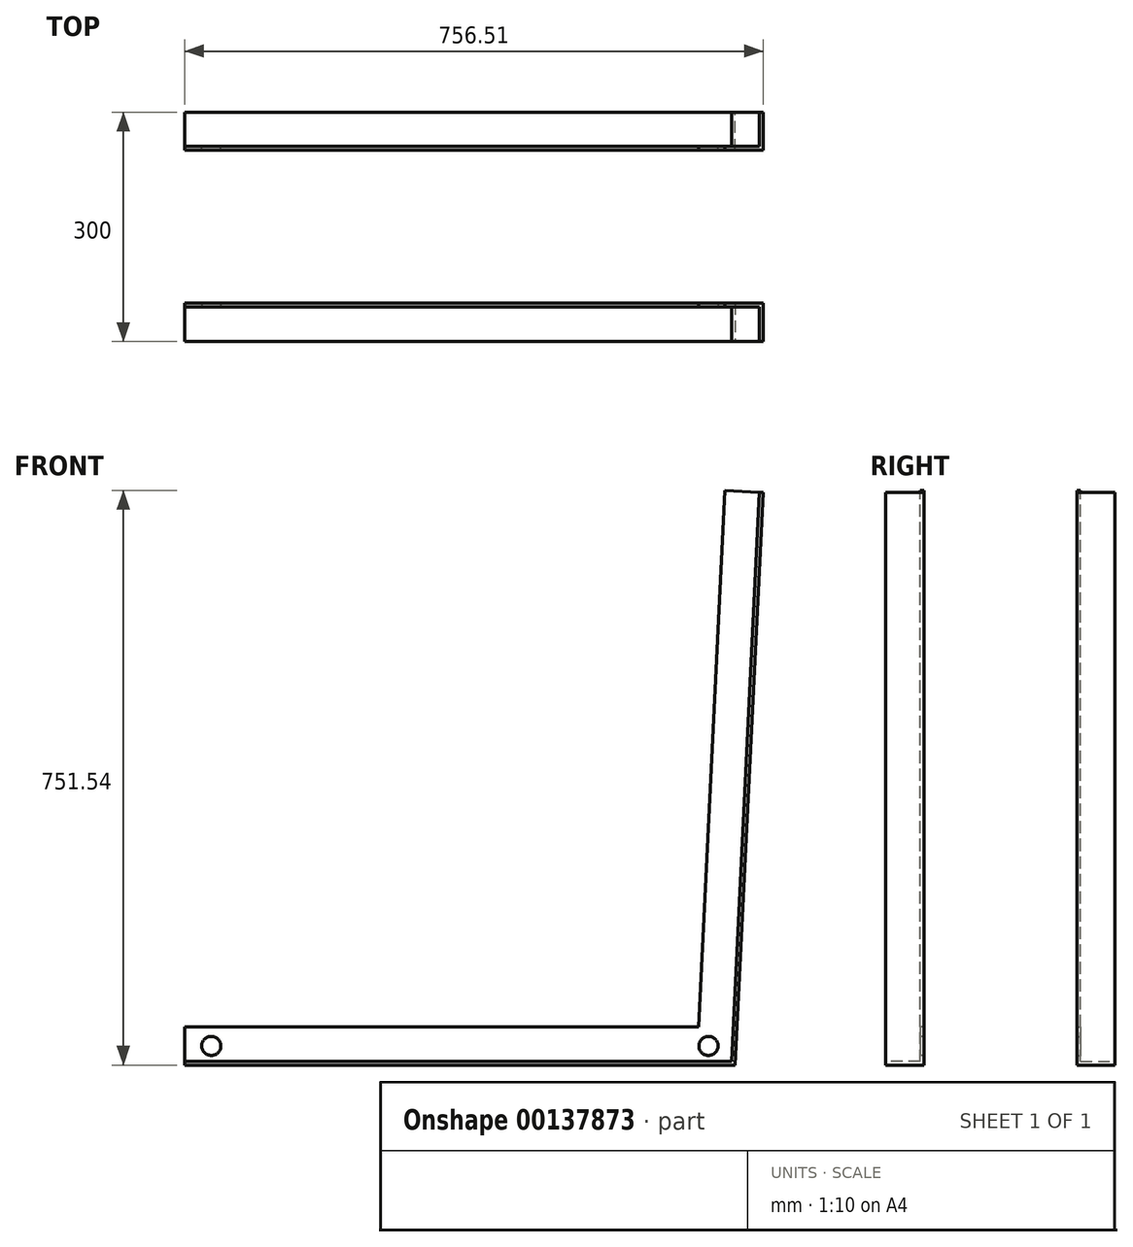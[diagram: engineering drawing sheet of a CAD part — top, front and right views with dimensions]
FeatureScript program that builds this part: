
annotation { "Feature Type Name" : "Feature", "Feature Type Description" : "" }
export const myFeature = defineFeature(function(context is Context, id is Id, definition is map)
    precondition{}
    {
        {
            var Q0;
            Q0=qCreatedBy(makeId("Right.planeOp"),FACE);
            var sketch = newSketch(context, id + "F0", { "sketchPlane" : qUnion([Q0])});
            skLineSegment(sketch, "E0", {"start": v(100, 50) * mm, "end": v(105, 50) * mm});
            skLineSegment(sketch, "E1", {"start": v(105, 50) * mm, "end": v(105, 5) * mm});
            skLineSegment(sketch, "E2", {"start": v(105, 5) * mm, "end": v(150, 5) * mm});
            skLineSegment(sketch, "E3", {"start": v(150, 5) * mm, "end": v(150, 0) * mm});
            skLineSegment(sketch, "E4", {"start": v(100, 50) * mm, "end": v(100, 0) * mm});
            skLineSegment(sketch, "E5", {"start": v(100, 0) * mm, "end": v(150, 0) * mm});
            skSolve(sketch);
        }
        {
            var Q0;
            Q0=qCreatedBy(makeId("Front.planeOp"),FACE);
            var Q1;
            Q1=sQuery(id+"F0.wireOp",VERTEX,"E5.start");
            cPlane(context, id + "F1", {"entities" : qUnion([Q0, Q1]), "cplaneType" : CPlaneType.PLANE_POINT, "offset" : 25 * mm, "width" : 150 * mm, "height" : 150 * mm});
        }
        {
            var Q0;
            Q0=qCreatedBy(id+"F1.planeOp",FACE);
            var sketch = newSketch(context, id + "F2", { "sketchPlane" : qUnion([Q0])});
            skLineSegment(sketch, "E6", {"start": v(0, 0) * mm, "end": v(720, 0) * mm});
            skLineSegment(sketch, "E7", {"start": v(720, 0) * mm, "end": v(756.5, 749.11) * mm});
            skSolve(sketch);
        }
        {
            var Q0;
            Q0=makeQuery(id+"F0.imprint","IMPRINT",FACE,{"disambiguationData":[TD([[makeQuery(id+"F0.imprint","IMPRINT",EDGE,{"derivedFrom":sQuery(id+"F0.wireOp",EDGE,"E0")}),-1.0]])]});
            var Q1;
            Q1=sQuery(id+"F2.wireOp",EDGE,"E6");
            var Q2;
            Q2=sQuery(id+"F2.wireOp",EDGE,"E7");
            sweep(context, id + "F3", {"profiles" : qUnion([Q0]), "path" : qUnion([Q1, Q2])});
        }
        {
            var Q0;
            Q0=makeQuery(id+"F7.opPattern","COPY",VERTEX,{"derivedFrom":makeQuery(id+"F3.opSweep","MID_CAP_VERTEX",VERTEX,{"disambiguationData":[OSD([sQuery(id+"F0.wireOp",EDGE,"E4"),sQuery(id+"F0.wireOp",EDGE,"E5"),sQuery(id+"F2.wireOp",EDGE,"E6")])],"capPos":1.0}),"instanceName":"1"});
            var Q1;
            Q1=makeQuery(id+"F7.opPattern","COPY",EDGE,{"derivedFrom":makeQuery(id+"F3.opSweep","SWEPT_EDGE",EDGE,{"disambiguationData":[OSD([sQuery(id+"F0.wireOp",EDGE,"E4"),sQuery(id+"F0.wireOp",EDGE,"E5"),sQuery(id+"F2.wireOp",EDGE,"E6")])]}),"instanceName":"1"});
            var Q2;
            Q2=makeQuery(id+"F3.opSweep","MID_CAP_VERTEX",VERTEX,{"disambiguationData":[OSD([sQuery(id+"F0.wireOp",EDGE,"E4"),sQuery(id+"F0.wireOp",EDGE,"E5"),sQuery(id+"F2.wireOp",EDGE,"E6")])],"capPos":1.0});
            var Q3;
            Q3=makeQuery(id+"F3.opSweep","SWEPT_EDGE",EDGE,{"disambiguationData":[OSD([sQuery(id+"F0.wireOp",EDGE,"E4"),sQuery(id+"F0.wireOp",EDGE,"E5"),sQuery(id+"F2.wireOp",EDGE,"E6")])]});
            cPlane(context, id + "F4", {"entities" : qUnion([Q0, Q1, Q2, Q3]), "cplaneType" : CPlaneType.LINE_POINT, "offset" : 25 * mm, "width" : 150 * mm, "height" : 150 * mm});
        }
        {
            var Q0;
            Q0=makeQuery(id+"F3.opSweep","SWEPT_FACE",FACE,{"disambiguationData":[OSD([sQuery(id+"F0.wireOp",EDGE,"E4"),sQuery(id+"F2.wireOp",EDGE,"E6")])]});
            var sketch = newSketch(context, id + "F5", { "sketchPlane" : qUnion([Q0])});
            skPoint(sketch, "E8", {"position": v(35, 25) * mm});
            skPoint(sketch, "E9", {"position": v(685, 25) * mm});
            skSolve(sketch);
        }
        {
            var Q0;
            Q0=sQuery(id+"F5.wireOp",VERTEX,"E8");
            var Q1;
            Q1=sQuery(id+"F5.wireOp",VERTEX,"E9");
            var Q2;
            Q2=makeQuery(id+"F3.opSweep","SWEPT_BODY",BODY,{"disambiguationData":[OSD([sQuery(id+"F0.wireOp",EDGE,"E0"),sQuery(id+"F0.wireOp",EDGE,"E1"),sQuery(id+"F0.wireOp",EDGE,"E2"),sQuery(id+"F0.wireOp",EDGE,"E3"),sQuery(id+"F0.wireOp",EDGE,"E4"),sQuery(id+"F0.wireOp",EDGE,"E5"),sQuery(id+"F2.wireOp",EDGE,"E7")])]});
            hole(context, id + "F6", {"style" : HoleStyle.SIMPLE, "endStyle" : HoleEndStyle.THROUGH, "holeDiameter" : 25 * mm, "locations" : qUnion([Q0, Q1]), "scope" : qUnion([Q2]), "tappedDepth" : 12 * mm, "tapClearance" : 3, "startStyle" : HoleStartStyle.PART});
        }
        {
            var Q0;
            Q0=makeQuery(id+"F3.opSweep","SWEPT_BODY",BODY,{"disambiguationData":[OSD([sQuery(id+"F0.wireOp",EDGE,"E0"),sQuery(id+"F0.wireOp",EDGE,"E1"),sQuery(id+"F0.wireOp",EDGE,"E2"),sQuery(id+"F0.wireOp",EDGE,"E3"),sQuery(id+"F0.wireOp",EDGE,"E4"),sQuery(id+"F0.wireOp",EDGE,"E5"),sQuery(id+"F2.wireOp",EDGE,"E7")])]});
            var Q1;
            Q1=qCreatedBy(makeId("Front.planeOp"),FACE);
            mirror(context, id + "F7", {"entities" : qUnion([Q0]), "mirrorPlane" : qUnion([Q1])});
        }
    });
